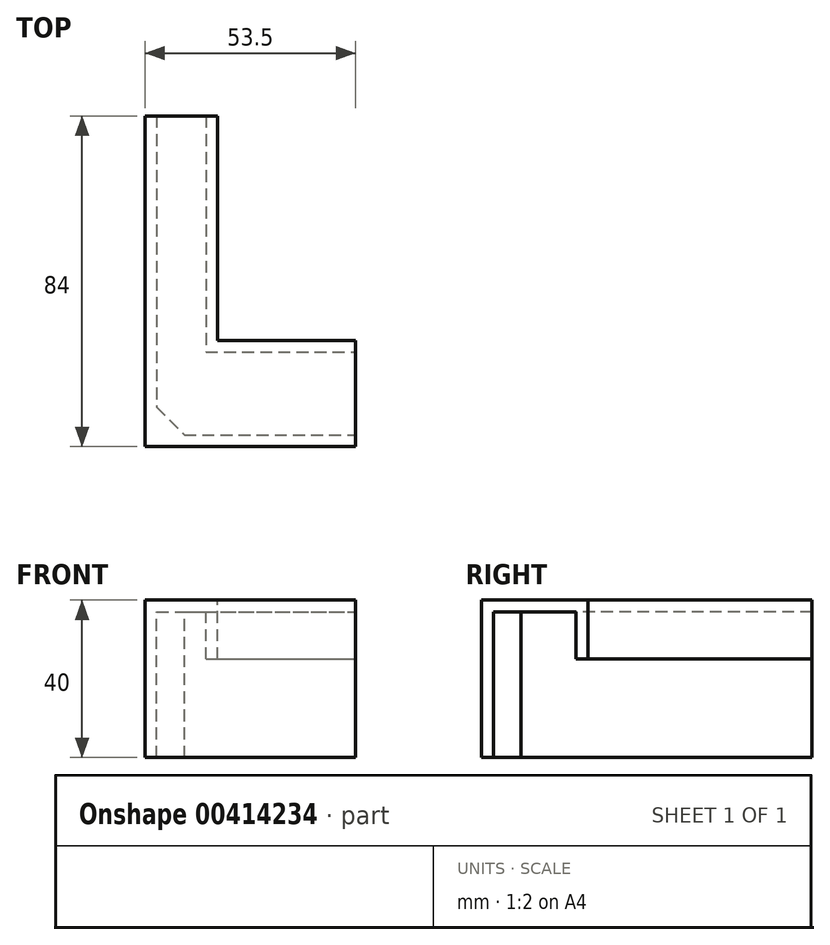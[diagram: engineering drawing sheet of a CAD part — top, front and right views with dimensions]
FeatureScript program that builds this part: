
annotation { "Feature Type Name" : "Feature", "Feature Type Description" : "" }
export const myFeature = defineFeature(function(context is Context, id is Id, definition is map)
    precondition{}
    {
        {
            var Q0;
            Q0=qCreatedBy(makeId("Top.planeOp"),FACE);
            var sketch = newSketch(context, id + "F0", { "sketchPlane" : qUnion([Q0])});
            skLineSegment(sketch, "E0", {"start": v(-12.5, 60) * mm, "end": v(0, 60) * mm});
            skLineSegment(sketch, "E1", {"start": v(0, 60) * mm, "end": v(0, 0) * mm});
            skLineSegment(sketch, "E2", {"start": v(0, 0) * mm, "end": v(45, 0) * mm});
            skLineSegment(sketch, "E3", {"start": v(45, 0) * mm, "end": v(45, -21) * mm});
            skLineSegment(sketch, "E4", {"start": v(-12.5, 60) * mm, "end": v(-12.5, -21) * mm});
            skLineSegment(sketch, "E5", {"start": v(-12.5, -21) * mm, "end": v(45, -21) * mm});
            skSolve(sketch);
        }
        {
            var Q0;
            Q0=qCreatedBy(makeId("Top.planeOp"),FACE);
            var sketch = newSketch(context, id + "F1", { "sketchPlane" : qUnion([Q0])});
            skLineSegment(sketch, "E6", {"start": v(-12.5, 60) * mm, "end": v(0, 60) * mm});
            skLineSegment(sketch, "E7", {"start": v(0, 60) * mm, "end": v(0, 0) * mm});
            skLineSegment(sketch, "E8", {"start": v(0, 0) * mm, "end": v(38, 0) * mm});
            skLineSegment(sketch, "E9", {"start": v(38, 0) * mm, "end": v(38, -21) * mm});
            skLineSegment(sketch, "E10", {"start": v(-12.5, 60) * mm, "end": v(-12.5, -21) * mm});
            skLineSegment(sketch, "E11", {"start": v(-12.5, -21) * mm, "end": v(38, -21) * mm});
            skLineSegment(sketch, "E12", {"start": v(-12.5, 60) * mm, "end": v(-15.5, 60) * mm});
            skLineSegment(sketch, "E13", {"start": v(-15.5, 60) * mm, "end": v(-15.5, -24) * mm});
            skLineSegment(sketch, "E14", {"start": v(-15.5, -24) * mm, "end": v(38, -24) * mm});
            skLineSegment(sketch, "E15", {"start": v(38, -24) * mm, "end": v(38, -21) * mm});
            skLineSegment(sketch, "E16", {"start": v(0, 60) * mm, "end": v(3, 60) * mm});
            skLineSegment(sketch, "E17", {"start": v(3, 60) * mm, "end": v(3, 3) * mm});
            skLineSegment(sketch, "E18", {"start": v(3, 3) * mm, "end": v(38, 3) * mm});
            skLineSegment(sketch, "E19", {"start": v(38, 3) * mm, "end": v(38, 0) * mm});
            skSolve(sketch);
        }
        {
            var Q0;
            Q0=makeQuery(id+"F1.imprint","IMPRINT",FACE,{"disambiguationData":[TD([[makeQuery(id+"F1.imprint","IMPRINT",EDGE,{"derivedFrom":sQuery(id+"F1.wireOp",EDGE,"E6")}),-1.0]])]});
            extrude(context, id + "F2", {"entities" : qUnion([Q0]), "oppositeDirection" : true, "depth" : 3 * mm});
        }
        {
            var Q0;
            Q0=makeQuery(id+"F1.imprint","IMPRINT",FACE,{"disambiguationData":[TD([[makeQuery(id+"F1.imprint","IMPRINT",EDGE,{"derivedFrom":sQuery(id+"F1.wireOp",EDGE,"E10")}),-1.0]])]});
            extrude(context, id + "F3", {"entities" : qUnion([Q0]), "operationType" : NewBodyOperationType.ADD, "oppositeDirection" : true, "depth" : 40 * mm});
        }
        {
            var Q0;
            Q0=makeQuery(id+"F1.imprint","IMPRINT",FACE,{"disambiguationData":[TD([[makeQuery(id+"F1.imprint","IMPRINT",EDGE,{"derivedFrom":sQuery(id+"F1.wireOp",EDGE,"E7")}),1.0]])]});
            extrude(context, id + "F4", {"entities" : qUnion([Q0]), "operationType" : NewBodyOperationType.ADD, "oppositeDirection" : true, "depth" : 15 * mm});
        }
        {
            var Q0;
            Q0=makeQuery(id+"F3.opExtrude","SWEPT_EDGE",EDGE,{"disambiguationData":[OSD([sQuery(id+"F1.wireOp",EDGE,"E10"),sQuery(id+"F1.wireOp",EDGE,"E11")])]});
            chamfer(context, id + "F5", {"entities" : qUnion([Q0]), "width" : 7 * mm, "tangentPropagation" : true});
        }
    });
